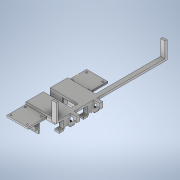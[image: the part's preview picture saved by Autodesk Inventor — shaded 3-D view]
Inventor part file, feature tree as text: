
AUTODESK INVENTOR PART (.ipt)
format: ipt  version: 2020.2 (Build 242310000, 310)  size: 916,480 bytes
history: native  units: mm
features: sketch x35, extrude x35, projected_geometry x17, hole x3
ambient origin geometry x8: Origin, YZ Plane, XZ Plane, XY Plane, X Axis, Y Axis, Z Axis, Center Point
bodies: Solid1 (feature_tree)
feature tree (90):
  sketch  "Sketch1"  dims[d0=8.0mm d1=98.298mm]
  extrude  "Extrusion1"  Depth=98.298mm
  extrude  "Extrusion2"  Depth=4.0mm
  extrude  "Extrusion3"  Depth=4.0mm TaperAngle=0.0deg
  extrude  "Extrusion4"  Depth=34.0mm
  extrude  "Extrusion5"  Depth=12.7mm
  extrude  "Extrusion6"  Depth=25.0mm
  hole  "Hole1"  [1 undecoded]
  extrude  "Extrusion11"  TaperAngle=60.0deg  [1 undecoded]
  extrude  "Extrusion12"  TaperAngle=120.0deg  [1 undecoded]
  sketch  "Sketch16"  dims[d19=6.4262mm d20=120.0deg]
  extrude  "Extrusion13"  Depth=6.4262mm
  extrude  "Extrusion14"  Depth=6.4262mm
  sketch  "Sketch17"  dims[d21=120.0deg d22=6.4262mm]
  extrude  "Extrusion15"  Depth=25.4mm TaperAngle=0.0deg
  extrude  "Extrusion18"  Depth=12.8016mm
  extrude  "Extrusion19"  Depth=12.8016mm
  extrude  "Extrusion20"  Depth=10.0mm
  hole  "Hole2"  [1 undecoded]
  extrude  "Extrusion21"  Depth=2.0mm
  extrude  "Extrusion22"  Depth=2.0mm
  sketch  "Sketch27"  dims[d45=12.8016mm d46=2.0mm]
  extrude  "Extrusion23"  Depth=25.4mm
  extrude  "Extrusion24"  Depth=32.48mm
  extrude  "Extrusion25"  TaperAngle=90.0deg  [1 undecoded]
  sketch  "Sketch29"  dims[d79=51.53mm d80=32.48mm]
  extrude  "Extrusion26"  Depth=2.0mm
  extrude  "Extrusion27"  Depth=21.0mm
  extrude  "Extrusion28"  Depth=36.0mm TaperAngle=0.0deg
  extrude  "Extrusion29"  Depth=8.0mm
  extrude  "Extrusion30"  Depth=17.5mm
  extrude  "Extrusion32"  Depth=35.0mm
  extrude  "Extrusion38"  Depth=5.0mm
  extrude  "Extrusion39"  TaperAngle=90.0deg  [1 undecoded]
  extrude  "Extrusion40"  Depth=5.0mm
  hole  "Hole4"  [1 undecoded]
  extrude  "Extrusion43"  Depth=1.5mm
  extrude  "Extrusion44"  TaperAngle=0.0deg  [1 undecoded]
  extrude  "Extrusion45"  Depth=28.8036mm
  extrude  "Extrusion46"  Depth=12.7mm
  extrude  "Extrusion47"  Depth=12.7mm
  extrude  "Extrusion48"  TaperAngle=120.0deg  [1 undecoded]
  extrude  "Extrusion49"  Depth=12.7mm
  sketch  "Sketch2"  dims[d2=8.0mm d3=4.0mm]
  sketch  "Sketch3"  dims[d4=4.0mm d5=4.0mm d6=0.0mm]
  sketch  "Sketch4"  dims[d7=34.0mm d8=0.0mm d9=19.558mm]
  sketch  "Sketch5"  dims[d10=16.1125mm d11=12.7mm]
  sketch  "Sketch6"  dims[d12=25.0mm d13=0.0mm d14=7.2009mm]
  sketch  "Sketch14"  dims[d15=6.4135mm d16=12.827mm]
  projected_geometry  "Projected Loop2"
  sketch  "Sketch15"  dims[d17=6.4262mm d18=60.0deg]
  projected_geometry  "Projected Loop3"
  sketch  "Sketch18"  dims[d23=120.0deg d24=6.4262mm]
  sketch  "Sketch21"  dims[d25=120.0deg d26=25.4mm d27=0.0mm]
  sketch  "Sketch22"  dims[d28=6.0mm d29=12.8016mm]
  sketch  "Sketch23"  dims[d30=5.9944mm d31=12.8016mm]
  sketch  "Sketch24"  dims[d32=25.4mm d33=0.0mm d34=10.0mm]
  sketch  "Sketch25"  dims[d35=90.0deg d36=20.0mm]
  projected_geometry  "Projected Loop5"
  sketch  "Sketch26"  dims[d37=3.4mm d38=19.05mm d39=6.2992mm d40=6.35mm d41=90.0deg d42=5.0mm d43=0.0mm d44=2.0mm]
  sketch  "Sketch28"  dims[d47=25.4mm d48=0.0mm d78=16.24mm]
  sketch  "Sketch30"  dims[d81=90.0deg d82=90.0deg]
  sketch  "Sketch32"  dims[d83=4.0mm d84=0.0mm d87=2.0mm]
  projected_geometry  "Projected Loop6"
  sketch  "Sketch33"  dims[d88=2.0mm d89=21.0mm]
  projected_geometry  "Projected Loop7"
  sketch  "Sketch35"  dims[d90=2.0mm d91=36.0mm d92=0.0mm]
  projected_geometry  "Projected Loop8"
  sketch  "Sketch42"  dims[d93=17.78mm d94=8.0mm]
  sketch  "Sketch43"  dims[d95=180.0deg d96=17.5mm]
  projected_geometry  "Projected Loop9"
  projected_geometry  "Projected Loop10"
  projected_geometry  "Projected Loop11"
  projected_geometry  "Projected Loop12"
  sketch  "Sketch44"  dims[d97=90.0deg d98=35.0mm]
  sketch  "Sketch45"  dims[d99=3.5mm d100=5.0mm]
  sketch  "Sketch48"  dims[d101=7.0mm d102=90.0deg]
  sketch  "Sketch49"  dims[d103=5.0mm d104=3.4mm]
  projected_geometry  "Projected Loop13"
  projected_geometry  "Projected Loop14"
  sketch  "Sketch50"  dims[d105=3.4mm d106=25.4mm d107=0.0mm]
  projected_geometry  "Projected Loop15"
  sketch  "Sketch51"  dims[d108=6.4262mm d109=0.0mm d110=1.5mm]
  sketch  "Sketch52"  dims[d111=1.5mm d112=0.0mm d113=0.0mm]
  sketch  "Sketch53"  dims[d128=44.8mm d129=28.8036mm]
  projected_geometry  "Projected Loop16"
  projected_geometry  "Projected Loop17"
  projected_geometry  "Projected Loop18"
  projected_geometry  "Projected Loop19"
  sketch  "Sketch54"  dims[d130=25.4mm d131=0.0mm d132=3.2131mm d133=6.4262mm d134=120.0deg d135=3.2131mm d136=6.4262mm d137=120.0deg d138=25.4mm d139=0.0mm d140=8.001mm d141=17.78mm d142=8.001mm d143=0.0mm d144=25.4mm d145=0.0mm d146=10.0mm d147=20.0mm d148=3.4mm d149=19.05mm d150=6.2992mm d151=6.35mm d152=90.0deg d153=5.0mm d154=0.0mm d155=16.2433mm d156=32.4866mm d157=51.5366mm d158=4.0mm d159=0.0mm d160=21.0mm d161=2.0mm d162=2.0mm d163=2.0mm d164=2.0mm d165=36.0mm d166=0.0mm d167=7.0mm d168=5.0mm d169=5.0mm d170=17.5mm d171=35.0mm d172=3.4mm d173=3.4mm d174=5.0mm d175=0.0mm d176=5.0mm d177=0.0mm d178=1.5mm d179=1.5mm d180=25.4mm d181=0.0mm d182=19.05mm d183=10.0mm d184=5.08mm d185=4.0mm d186=0.0mm d187=10.0mm d188=0.0mm d189=2.0mm d190=3.0mm d191=25.4mm d192=0.0mm d194=30.0mm d195=0.0mm d196=102.489mm d197=0.0mm d201=11.43mm d202=0.0mm d239=25.4mm d240=0.0mm d241=1.5mm d242=0.0mm d243=39.0mm d244=35.0mm d245=39.0mm d246=35.0mm d247=3.0mm d248=0.0mm d249=5.0mm d250=5.0mm d251=29.7mm d252=26.05mm d253=4.0mm d254=4.0mm d255=29.7mm d256=26.05mm d257=3.4mm d258=19.05mm d259=6.2992mm d260=6.35mm d261=90.0deg d262=25.4mm d263=20.594885mm d271=4.0mm d272=28.4mm d273=0.0mm d274=25.4mm d275=0.0mm d276=3.429mm d277=180.0deg d278=30.0mm d279=0.0mm d280=6.35mm d281=25.4mm d282=0.0mm d283=5.08mm d284=25.4mm d285=0.0mm d286=2.0mm d287=0.0mm d288=12.7mm d289=0.0mm d214=12.7mm d215=0.872665mm d216=12.7mm d217=0.872665mm d228=12.7mm d229=0.872665mm d230=12.7mm d231=0.872665mm]
note: 9 required parameter values undecoded (feature->parameter linkage not recoverable at this tier; creation-order binding heuristic only, values carry confidence <= 0.55)
